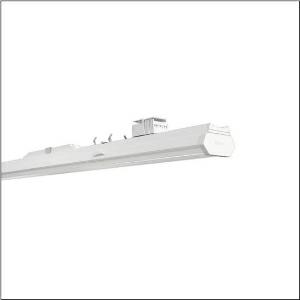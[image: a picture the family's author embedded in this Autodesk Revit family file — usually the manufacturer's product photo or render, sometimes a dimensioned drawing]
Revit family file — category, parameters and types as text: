
# Revit family: licross_r__21_protected_mo_52td12cn675f_4ad1
name_source: partatom
category: Lighting Fixtures
units: mm (PartAtom-declared; Revit-internal decimal feet)

## family parameters
Cut with Voids When Loaded = No
Host = Face
Light Source = No
Part Type = Normal
Room Calculation Point = No
Round Connector Dimension = Use Diameter
Shared = No

## types (1)
- --- (1 x LED, 7960 lm, 48.5 W, 6500K)
    Apparent Load = 49 VA
    CIE Flux Codes = 73 92 98 99 100
    Color Rendering = 80
    Color Temperature = 6500K
    Default Elevation = 1800 mm
    Description = Licross® 21 Protected MO, luminaire insert, of sheet steel, galvanised, coil coated, white, length: 1.500mm, width: 90mm, height: 101mm, LED rated luminous flux: 7.940lm, light colour: 865, control gear: ON/OFF Multilumen, CLOi, control gear: ECG Multilumen, with plug, 3-pole, with phase selection, mains connection: 220..240V, AC, 50/60Hz, halogen-free wiring, primary optical cover: cover, of PMMA, light emission: direct with ceiling illumination distribution, protection rating (complete): IP54, insulation class (complete): insulation class I (protective earthing), certification: CE, ENEC, VDE, UKCA, protection symbol: D if used in an environment with non-conductive dust loads with corresponding accessories, permissible ambient temperature for indoor applications: -35..+45°C, corresponds to IFS (International Featured Standards) requirements for safety and quality in the food industry, reducing of maximum allowable ambient temperature of 5°C with ceiling mounting, LABS conformity tested according to VDMA 24364:2018-05, packaging unit: 1 piece
    Height = 92 mm
    Lamp = 1 x LED
    Lamp Light Flux = 7960 lm
    Lamp Power = 48.5 W
    Lamp count = 1
    Length = 1500 mm
    Luminous efficacy = 164 lm/W
    Manufacturer = Siteco
    ModVariant = No
    Model = 52TD12CN675F
    Mounting Place = Ceiling
    Mounting Type = Pendant
    Number of Poles = 1
    OnlyDefault = Yes
    Power Factor = 1
    Product Name = Licross® 21 Protected MO
    Product group = luminaire insert
    ProductGroupID = 902
    Protection Class = Protection class I
    Protection Degree = IP 54
    RLX_Detail_Level = 1
    RlxData = <blob elided: 21937 chars, md5=885ae365>
    Socket = socket
    Standby Power = 0 W
    System Light Flux = 7960 lm
    System Power = 49 W
    Type Comments = factory setting: luminous flux: 100 % | (A | C | E) | 117 mA
    Type Image = l_1256148.jpg
    URL = http://relux.com
    VarID = @adj_118499
    Voltage = 0 V
    Weight = 0.00 kg
    Width = 88 mm

## geometry (parser evidence)
native form markers: Blend x4, Sweep x11
no freeform markers — native parametric forms only
